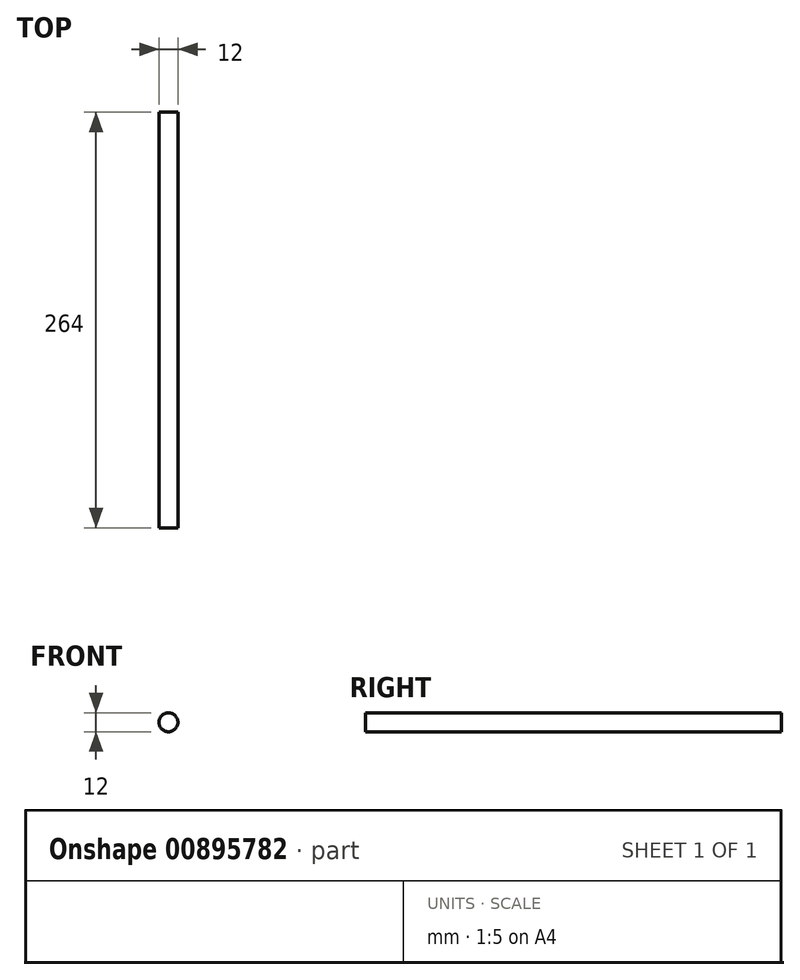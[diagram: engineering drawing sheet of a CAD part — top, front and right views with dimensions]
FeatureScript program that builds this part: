
annotation { "Feature Type Name" : "Feature", "Feature Type Description" : "" }
export const myFeature = defineFeature(function(context is Context, id is Id, definition is map)
    precondition{}
    {
        {
            var Q0;
            Q0=qCreatedBy(makeId("Front.planeOp"),FACE);
            var sketch = newSketch(context, id + "F0", { "sketchPlane" : qUnion([Q0])});
            skCircle(sketch, "E0", {"center": v(0, 0) * mm, "radius": 6 * mm});
            skSolve(sketch);
        }
        {
            var Q0;
            Q0=qSketchRegion(id+"F0",true);
            extrude(context, id + "F1", {"entities" : qUnion([Q0]), "offsetDistance" : 25 * mm, "depth" : 264 * mm});
        }
    });
